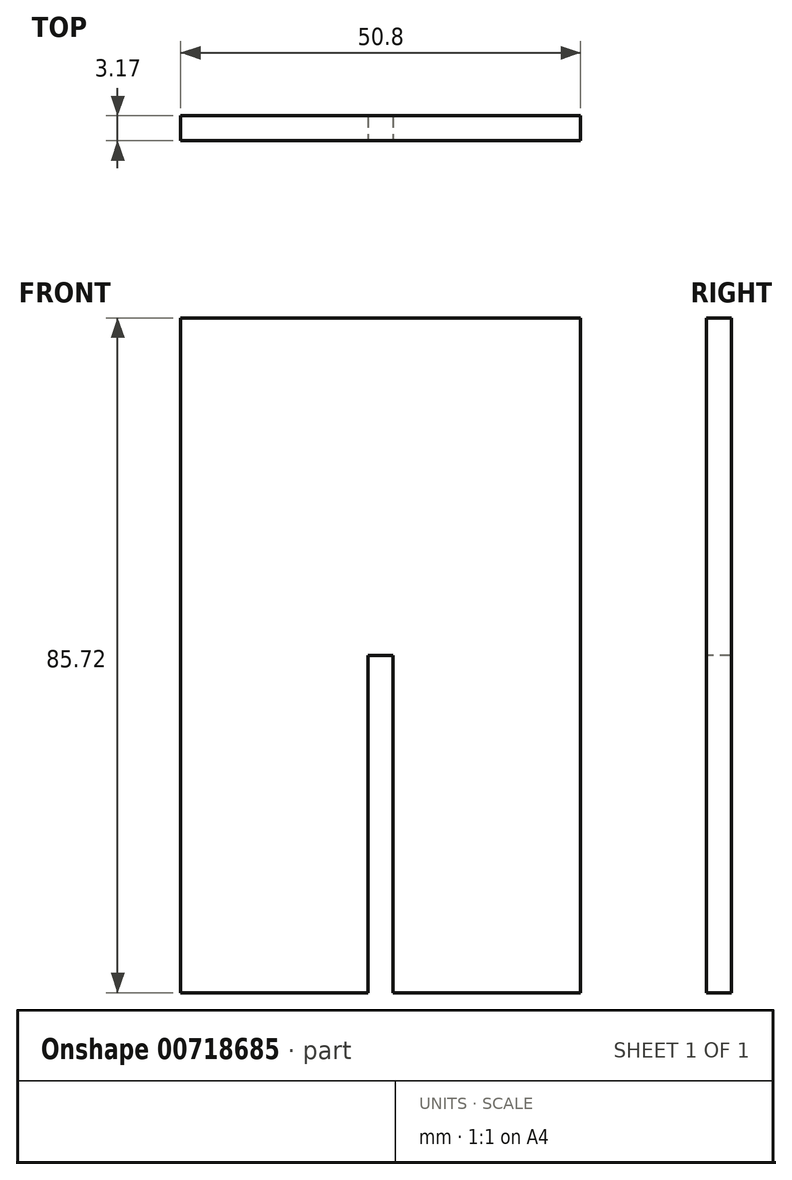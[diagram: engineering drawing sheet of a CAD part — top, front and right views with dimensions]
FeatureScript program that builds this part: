
annotation { "Feature Type Name" : "Feature", "Feature Type Description" : "" }
export const myFeature = defineFeature(function(context is Context, id is Id, definition is map)
    precondition{}
    {
        {
            var Q0;
            Q0=qCreatedBy(makeId("Front.planeOp"),FACE);
            var sketch = newSketch(context, id + "F0", { "sketchPlane" : qUnion([Q0])});
            skLineSegment(sketch, "E0.bottom", {"start": v(32.34, 42.86) * mm, "end": v(-18.46, 42.86) * mm});
            skLineSegment(sketch, "E0.top", {"start": v(32.34, -42.86) * mm, "end": v(-18.46, -42.86) * mm});
            skLineSegment(sketch, "E0.left", {"start": v(32.34, 42.86) * mm, "end": v(32.34, -42.86) * mm});
            skLineSegment(sketch, "E0.right", {"start": v(-18.46, 42.86) * mm, "end": v(-18.46, -42.86) * mm});
            skPoint(sketch, "E0.middle", {"position": v(6.94, 0) * mm});
            skSolve(sketch);
        }
        {
            var Q0;
            Q0 = qSketchRegion(id + "F0", true);
            extrude(context, id + "F1", {"entities" : qUnion([Q0]), "depth" : 3.17 * mm, "offsetDistance" : 25.4 * mm});
        }
        {
            var Q0;
            Q0=makeQuery(id+"F1.opExtrude","CAP_FACE",FACE,{"disambiguationData":[OSD([sQuery(id+"F0.wireOp",EDGE,"E0.bottom"),sQuery(id+"F0.wireOp",EDGE,"E0.top"),sQuery(id+"F0.wireOp",EDGE,"E0.left"),sQuery(id+"F0.wireOp",EDGE,"E0.right")])],"isStart":false});
            var sketch = newSketch(context, id + "F2", { "sketchPlane" : qUnion([Q0])});
            skLineSegment(sketch, "E1.bottom", {"start": v(5.35, -42.86) * mm, "end": v(8.53, -42.86) * mm});
            skLineSegment(sketch, "E1.top", {"start": v(5.35, 0) * mm, "end": v(8.53, 0) * mm});
            skLineSegment(sketch, "E1.left", {"start": v(5.35, -42.86) * mm, "end": v(5.35, 0) * mm});
            skLineSegment(sketch, "E1.right", {"start": v(8.53, -42.86) * mm, "end": v(8.53, 0) * mm});
            skSolve(sketch);
        }
        {
            var Q0;
            Q0 = qSketchRegion(id + "F2", true);
            extrude(context, id + "F3", {"entities" : qUnion([Q0]), "operationType" : NewBodyOperationType.REMOVE, "endBound" : BoundingType.THROUGH_ALL, "oppositeDirection" : true, "depth" : 25.4 * mm, "offsetDistance" : 25.4 * mm});
        }
    });
